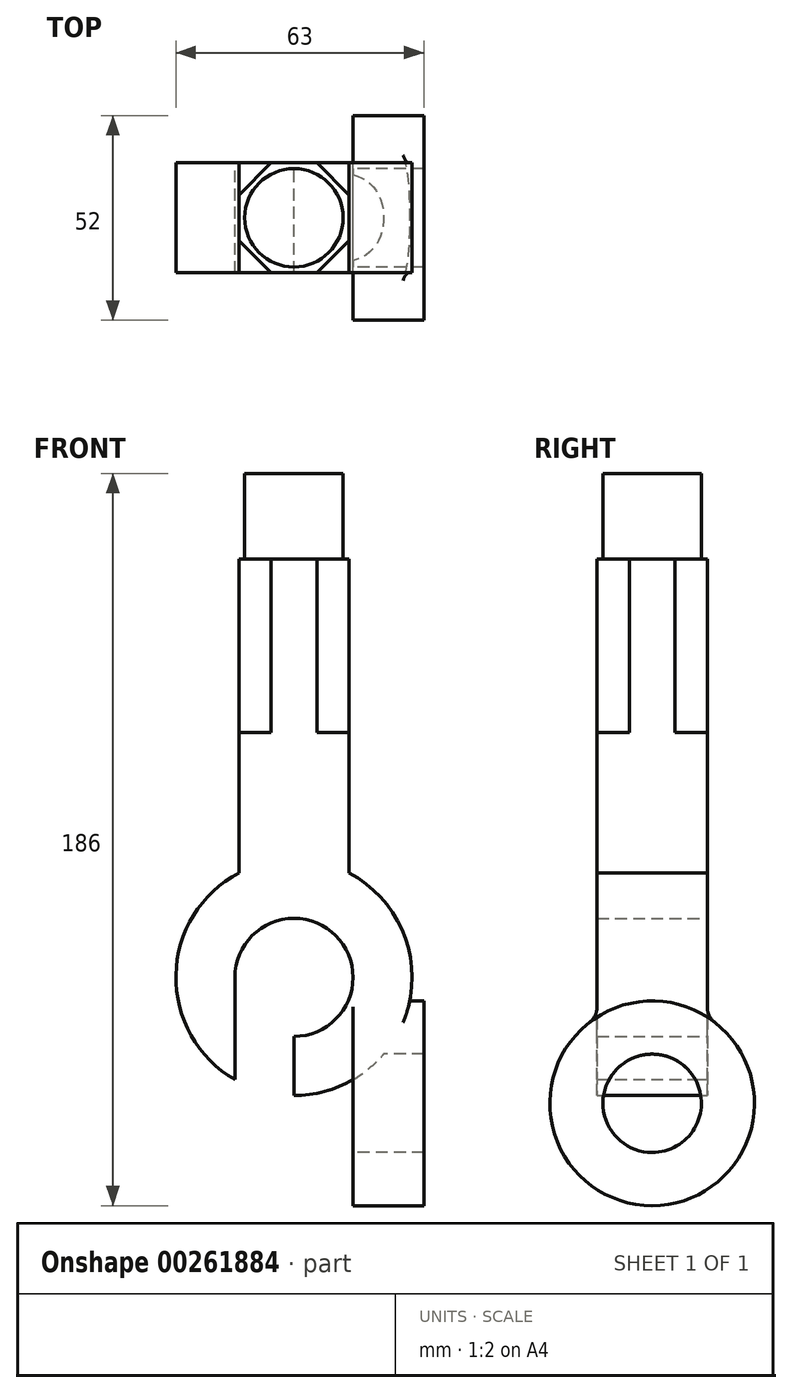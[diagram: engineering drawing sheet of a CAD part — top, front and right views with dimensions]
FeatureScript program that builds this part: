
annotation { "Feature Type Name" : "Feature", "Feature Type Description" : "" }
export const myFeature = defineFeature(function(context is Context, id is Id, definition is map)
    precondition{}
    {
        {
            var Q0;
            Q0=qCreatedBy(makeId("Front.planeOp"),FACE);
            var sketch = newSketch(context, id + "F0", { "sketchPlane" : qUnion([Q0])});
            skLineSegment(sketch, "E0.bottom", {"start": v(14, 35.73) * mm, "end": v(-14, 35.73) * mm});
            skLineSegment(sketch, "E0.top", {"start": v(14, -35.73) * mm, "end": v(-14, -35.73) * mm, "construction": true});
            skLineSegment(sketch, "E0.left", {"start": v(14, 35.73) * mm, "end": v(14, 0) * mm, "construction": true});
            skLineSegment(sketch, "E0.right", {"start": v(-14, 35.73) * mm, "end": v(-14, 0) * mm, "construction": true});
            skPoint(sketch, "E0.middle", {"position": v(0, 0) * mm});
            skCircle(sketch, "E1", {"center": v(0, -62.27) * mm, "radius": 30 * mm});
            skCircle(sketch, "E2", {"center": v(0, -62.27) * mm, "radius": 15 * mm});
            skLineSegment(sketch, "E3", {"start": v(-29.4, -68.27) * mm, "end": v(-29.4, -120.27) * mm, "construction": true});
            skLineSegment(sketch, "E4", {"start": v(-29.4, -120.27) * mm, "end": v(-11.4, -120.27) * mm, "construction": true});
            skLineSegment(sketch, "E5", {"start": v(-11.4, -120.27) * mm, "end": v(-11.4, -90.02) * mm, "construction": true});
            skPoint(sketch, "E6", {"position": v(-29.4, -94.27) * mm});
            skLineSegment(sketch, "E7", {"start": v(0, 35.73) * mm, "end": v(0, 65.73) * mm});
            skPoint(sketch, "E7.endSnap0", {"position": v(0, 35.73) * mm});
            skLineSegment(sketch, "E8", {"start": v(0, 65.73) * mm, "end": v(12.5, 65.73) * mm});
            skLineSegment(sketch, "E9", {"start": v(12.5, 65.73) * mm, "end": v(12.5, 35.73) * mm});
            skLineSegment(sketch, "E10", {"start": v(-14, 0) * mm, "end": v(14, 0) * mm});
            skLineSegment(sketch, "E11", {"start": v(14, 0) * mm, "end": v(14, -35.73) * mm});
            skLineSegment(sketch, "E12", {"start": v(-14, 0) * mm, "end": v(-14, -35.73) * mm});
            skLineSegment(sketch, "E13", {"start": v(14, 0) * mm, "end": v(14, 0) * mm});
            skLineSegment(sketch, "E14", {"start": v(-48, -77.47) * mm, "end": v(-48, -156.02) * mm, "construction": true});
            skSolve(sketch);
        }
        {
            var Q0;
            Q0=makeQuery(id+"F0.imprint","IMPRINT",FACE,{"disambiguationData":[TD([[makeQuery(id+"F0.imprint","IMPRINT",EDGE,{"derivedFrom":sQuery(id+"F0.wireOp",EDGE,"E2")}),-1.0]])]});
            var Q1;
            {var subQ4=sQuery(id+"F0.wireOp",EDGE,"E10");Q1=makeQuery(id+"F0.imprint","IMPRINT",FACE,{"disambiguationData":[TD([[makeQuery(id+"F0.imprint","IMPRINT",EDGE,{"derivedFrom":subQ4}),-1.0]])]});}
            extrude(context, id + "F1", {"entities" : qUnion([Q0, Q1]), "endBound" : BoundingType.SYMMETRIC, "depth" : 28 * mm});
        }
        {
            var Q0;
            Q0=makeQuery(id+"F1.opExtrude","SWEPT_FACE",FACE,{"disambiguationData":[OSD([sQuery(id+"F0.wireOp",EDGE,"E10")])]});
            var sketch = newSketch(context, id + "F2", { "sketchPlane" : qUnion([Q0])});
            skCircle(sketch, "E15.cCircle", {"center": v(0, 0) * mm, "radius": 14 * mm, "construction": true});
            skLineSegment(sketch, "E15.0", {"start": v(5.8, 14) * mm, "end": v(14, 5.8) * mm});
            skLineSegment(sketch, "E15.1", {"start": v(14, 5.8) * mm, "end": v(14, -5.8) * mm});
            skLineSegment(sketch, "E15.2", {"start": v(14, -5.8) * mm, "end": v(5.8, -14) * mm});
            skLineSegment(sketch, "E15.3", {"start": v(5.8, -14) * mm, "end": v(-5.8, -14) * mm});
            skLineSegment(sketch, "E15.4", {"start": v(-5.8, -14) * mm, "end": v(-14, -5.8) * mm});
            skLineSegment(sketch, "E15.5", {"start": v(-14, -5.8) * mm, "end": v(-14, 5.8) * mm});
            skLineSegment(sketch, "E15.6", {"start": v(-14, 5.8) * mm, "end": v(-5.8, 14) * mm});
            skLineSegment(sketch, "E15.7", {"start": v(-5.8, 14) * mm, "end": v(5.8, 14) * mm});
            skPoint(sketch, "E15.0.midPoint", {"position": v(9.9, 9.9) * mm});
            skSolve(sketch);
        }
        {
            var Q0;
            Q0 = qSketchRegion(id + "F2", true);
            extrude(context, id + "F3", {"entities" : qUnion([Q0]), "operationType" : NewBodyOperationType.ADD, "depth" : 44 * mm});
        }
        {
            var Q0;
            {var subQ0=sQuery(id+"F0.wireOp",EDGE,"E7");Q0=makeQuery(id+"F0.imprint","IMPRINT",FACE,{"disambiguationData":[TD([[makeQuery(id+"F0.imprint","IMPRINT",EDGE,{"derivedFrom":subQ0}),-1.0]])]});}
            var Q1;
            Q1=sQuery(id+"F0.wireOp",EDGE,"E7");
            revolve(context, id + "F4", {"operationType" : NewBodyOperationType.ADD, "entities" : qUnion([Q0]), "axis" : qUnion([Q1]), "revolveType" : RevolveType.FULL});
        }
        {
            var Q0;
            Q0=qCreatedBy(makeId("Right.planeOp"),FACE);
            cPlane(context, id + "F5", {"entities" : qUnion([Q0]), "cplaneType" : CPlaneType.OFFSET, "offset" : 15 * mm, "width" : 150 * mm, "height" : 150 * mm});
        }
        {
            var Q0;
            Q0=qCreatedBy(id+"F5.planeOp",FACE);
            var sketch = newSketch(context, id + "F6", { "sketchPlane" : qUnion([Q0])});
            skPoint(sketch, "E16.0", {"position": v(0, -94.27) * mm});
            skCircle(sketch, "E17", {"center": v(0, -94.27) * mm, "radius": 26 * mm});
            skCircle(sketch, "E18", {"center": v(0, -94.27) * mm, "radius": 12.5 * mm});
            skSolve(sketch);
        }
        {
            var Q0;
            Q0 = qSketchRegion(id + "F6", true);
            extrude(context, id + "F7", {"entities" : qUnion([Q0]), "operationType" : NewBodyOperationType.ADD, "depth" : 18 * mm});
        }
        {
            var Q0;
            Q0=qCreatedBy(makeId("Front.planeOp"),FACE);
            var sketch = newSketch(context, id + "F8", { "sketchPlane" : qUnion([Q0])});
            skPoint(sketch, "E19.0", {"position": v(0, -62.27) * mm});
            skLineSegment(sketch, "E20", {"start": v(0, -62.27) * mm, "end": v(-15, -62.27) * mm});
            skLineSegment(sketch, "E21.0", {"start": v(-15, -72.36) * mm, "end": v(-15, -94.27) * mm});
            skPoint(sketch, "E22.0", {"position": v(-29.4, -94.27) * mm});
            skLineSegment(sketch, "E23", {"start": v(-15, -62.27) * mm, "end": v(-15, -94.27) * mm});
            skLineSegment(sketch, "E24", {"start": v(-15, -94.27) * mm, "end": v(0, -94.27) * mm});
            skLineSegment(sketch, "E25", {"start": v(0, -94.27) * mm, "end": v(0, -62.27) * mm});
            skPoint(sketch, "E26.orphan", {"position": v(-15, -120.27) * mm});
            skSolve(sketch);
        }
        {
            var Q0;
            Q0 = qSketchRegion(id + "F8", true);
            extrude(context, id + "F9", {"entities" : qUnion([Q0]), "operationType" : NewBodyOperationType.REMOVE, "endBound" : BoundingType.SYMMETRIC, "depth" : 40 * mm});
        }
        {
            var Q0;
            Q0=makeQuery(id+"FIrYsT40nQyqnbh_1.1.F7.boolean.opBoolean","INTERSECT",EDGE,{"derivedFrom":[makeQuery(id+"F3.boolean.opBoolean","MERGE",FACE,{"derivedFrom":[makeQuery(id+"F1.opExtrude","CAP_FACE",FACE,{"disambiguationData":[OSD([sQuery(id+"F0.wireOp",EDGE,"E1"),sQuery(id+"F0.wireOp",EDGE,"E2"),sQuery(id+"F0.wireOp",EDGE,"E10"),sQuery(id+"F0.wireOp",EDGE,"E11"),sQuery(id+"F0.wireOp",EDGE,"E12")])],"isStart":false}),makeQuery(id+"F3.opExtrude","SWEPT_FACE",FACE,{"disambiguationData":[OSD([sQuery(id+"F2.wireOp",EDGE,"E15.3")])]})]}),makeQuery(id+"FIrYsT40nQyqnbh_1.1.F7.opExtrude","SWEPT_FACE",FACE,{"disambiguationData":[OSD([sQuery(id+"F6.wireOp",EDGE,"E17")])]})]});
            var Q1;
            Q1=makeQuery(id+"F7.boolean.opBoolean","INTERSECT",EDGE,{"derivedFrom":[makeQuery(id+"F3.boolean.opBoolean","MERGE",FACE,{"derivedFrom":[makeQuery(id+"F1.opExtrude","CAP_FACE",FACE,{"disambiguationData":[OSD([sQuery(id+"F0.wireOp",EDGE,"E1"),sQuery(id+"F0.wireOp",EDGE,"E2"),sQuery(id+"F0.wireOp",EDGE,"E10"),sQuery(id+"F0.wireOp",EDGE,"E11"),sQuery(id+"F0.wireOp",EDGE,"E12")])],"isStart":false}),makeQuery(id+"F3.opExtrude","SWEPT_FACE",FACE,{"disambiguationData":[OSD([sQuery(id+"F2.wireOp",EDGE,"E15.3")])]})]}),makeQuery(id+"F7.opExtrude","SWEPT_FACE",FACE,{"disambiguationData":[OSD([sQuery(id+"F6.wireOp",EDGE,"E17")])]})]});
            var Q2;
            Q2=makeQuery(id+"F7.boolean.opBoolean","INTERSECT",EDGE,{"derivedFrom":[makeQuery(id+"F3.boolean.opBoolean","MERGE",FACE,{"derivedFrom":[makeQuery(id+"F1.opExtrude","CAP_FACE",FACE,{"disambiguationData":[OSD([sQuery(id+"F0.wireOp",EDGE,"E1"),sQuery(id+"F0.wireOp",EDGE,"E2"),sQuery(id+"F0.wireOp",EDGE,"E10"),sQuery(id+"F0.wireOp",EDGE,"E11"),sQuery(id+"F0.wireOp",EDGE,"E12")])],"isStart":true}),makeQuery(id+"F3.opExtrude","SWEPT_FACE",FACE,{"disambiguationData":[OSD([sQuery(id+"F2.wireOp",EDGE,"E15.7")])]})]}),makeQuery(id+"F7.opExtrude","SWEPT_FACE",FACE,{"disambiguationData":[OSD([sQuery(id+"F6.wireOp",EDGE,"E17")])]})]});
            var Q3;
            Q3=makeQuery(id+"FIrYsT40nQyqnbh_1.1.F7.boolean.opBoolean","INTERSECT",EDGE,{"derivedFrom":[makeQuery(id+"F3.boolean.opBoolean","MERGE",FACE,{"derivedFrom":[makeQuery(id+"F1.opExtrude","CAP_FACE",FACE,{"disambiguationData":[OSD([sQuery(id+"F0.wireOp",EDGE,"E1"),sQuery(id+"F0.wireOp",EDGE,"E2"),sQuery(id+"F0.wireOp",EDGE,"E10"),sQuery(id+"F0.wireOp",EDGE,"E11"),sQuery(id+"F0.wireOp",EDGE,"E12")])],"isStart":true}),makeQuery(id+"F3.opExtrude","SWEPT_FACE",FACE,{"disambiguationData":[OSD([sQuery(id+"F2.wireOp",EDGE,"E15.7")])]})]}),makeQuery(id+"FIrYsT40nQyqnbh_1.1.F7.opExtrude","SWEPT_FACE",FACE,{"disambiguationData":[OSD([sQuery(id+"F6.wireOp",EDGE,"E17")])]})]});
            fillet(context, id + "F10", {"entities" : qUnion([Q0, Q1, Q2, Q3]), "radius" : 5 * mm, "tangentPropagation" : true, "allowEdgeOverflow" : false});
        }
    });
